# Revit family: 1Electronics_Commercial-Audio_Biamp_Versatile-Music-Source_PC1000
name_source: partatom
category: Communication Devices
units: mm (PartAtom-declared; Revit-internal decimal feet)

## family parameters
Cut with Voids When Loaded = No
Host = Face
Maintain Annotation Orientation = No
OmniClass Number = 23.85.10.11.14
OmniClass Title = Audio Equipment
Part Type = Normal
Room Calculation Point = No
Round Connector Dimension = Use Diameter
Shared = No

## types (1)
- PC1000RMKII
    Apparent Load = 0 VA
    Applicable low impedance = Yes
    Balanced outputs = 2 x XLR
    CD = Yes
    Connector Description = 230VAC / 50-60Hz / 30VA MAX
    Default Elevation = 4' - 0"
    Depth = 1' - 0"
    Description = PC1000RMKII Versatile CD / USB / SD-Card Music Source
    Height = 0' - 1 1/2"
    Housing Material = Biamp - Metal - Black
    IR remote included = Yes
    Manufacturer = Biamp
    Max Power Consumption = 0 W
    Model = PC1000RMKII
    Number of Poles = 1
    Other/digital outputs = 1 x optical + 1 x coaxial
    Power Factor = 1
    Product Documentation Link = https://downloads.biamp.com
    Product Page URL = https://www.biamp.com
    Product data url = https://www.bimobject.com
    RS232 control = Yes
    SD card = 32 GB up to 9999 songs
    Supported file format = MP3, WMA
    URL = https://www.biamp.com
    USB = 32 GB up to 9999 songs
    Unbalanced outputs = 2 x RCA
    Voltage = 230 V
    Weight = 9.90 lbf
    Width = 1' - 7"

## geometry (parser evidence)
native form markers: Sweep x4
no freeform markers — native parametric forms only
